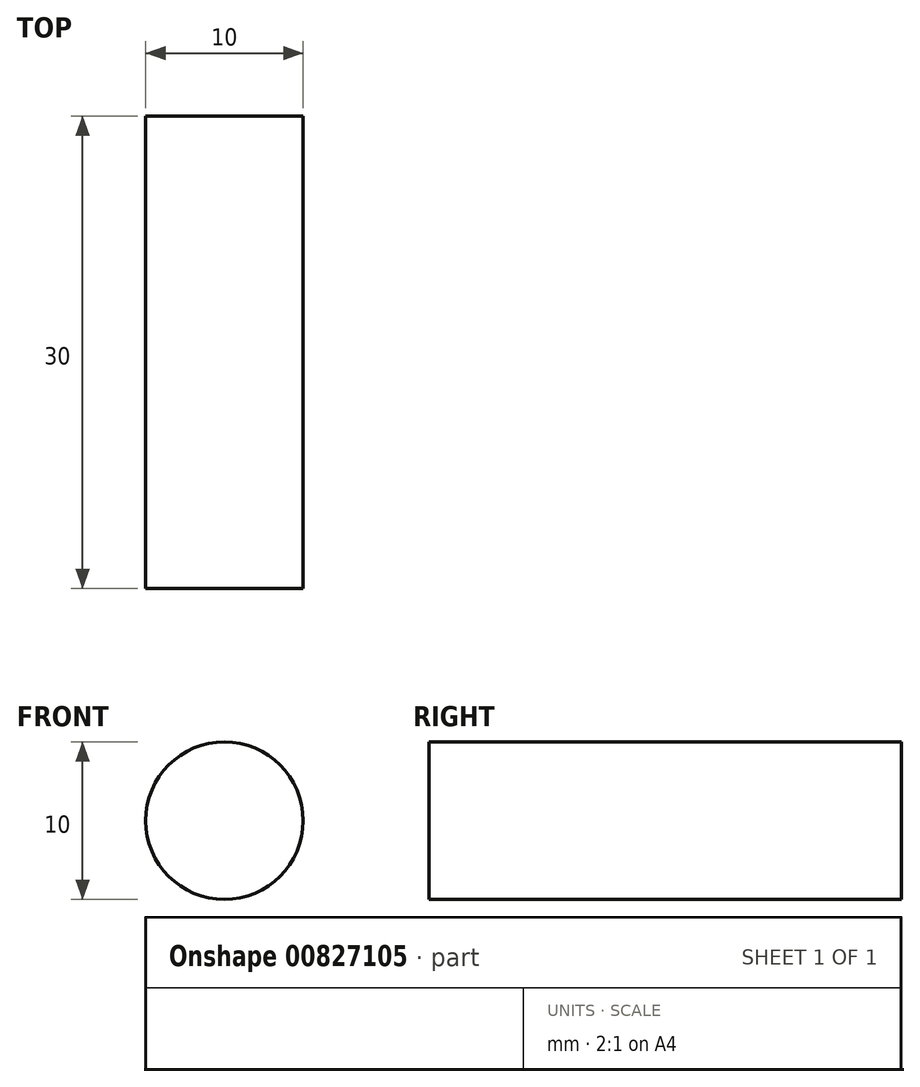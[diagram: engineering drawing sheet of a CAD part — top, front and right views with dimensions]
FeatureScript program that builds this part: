
annotation { "Feature Type Name" : "Feature", "Feature Type Description" : "" }
export const myFeature = defineFeature(function(context is Context, id is Id, definition is map)
    precondition{}
    {
        {
            var Q0;
            Q0=qCreatedBy(makeId("Front.planeOp"),FACE);
            var sketch = newSketch(context, id + "F0", { "sketchPlane" : qUnion([Q0])});
            skCircle(sketch, "E0", {"center": v(0, 0) * mm, "radius": 5 * mm});
            skSolve(sketch);
        }
        {
            var Q0;
            Q0 = qSketchRegion(id + "F0", true);
            extrude(context, id + "F1", {"entities" : qUnion([Q0]), "depth" : 30 * mm, "offsetDistance" : 25 * mm});
        }
    });
